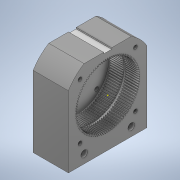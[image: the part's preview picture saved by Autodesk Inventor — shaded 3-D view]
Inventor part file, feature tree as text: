
AUTODESK INVENTOR PART (.ipt)
format: ipt  version: 2022 (Build 260153000, 153)  size: 1,526,272 bytes
history: mixed  units: mm
features: sketch x7, extrude x6, other x3, imported_body x1
ambient origin geometry x8: Origin, YZ Plane, XZ Plane, XY Plane, X Axis, Y Axis, Z Axis, Center Point
bodies: Solid1 (imported_parasolid)
feature tree (17):
  other  "Assembly2.iam"
  other  "96Gears_Stage_1_modified.ipt:1"
  other  "96Gears_Stage_2_modified.ipt:1"
  extrude  "Extrusion3"  Depth=3.0mm
  extrude  "Extrusion5"  Depth=1.0mm TaperAngle=0.0deg
  extrude  "Extrusion6"  Depth=6.0mm TaperAngle=0.0deg
  extrude  "Extrusion7"  TaperAngle=0.0deg  [1 undecoded]
  extrude  "Extrusion8"  Depth=3.5mm
  extrude  "Extrusion9"  Depth=5.0mm
  sketch  "Sketch5"  dims[d7=6.0mm d8=1.0mm d9=0.0mm]
  sketch  "Sketch4"  dims[d0=10.0mm d6=3.0mm]
  sketch  "Sketch7"  dims[d17=32.25mm d18=6.0mm d19=0.0mm]
  sketch  "Sketch8"  dims[d20=10.0mm d21=0.0mm d22=0.0mm]
  sketch  "Sketch9"  dims[d23=6.75mm d27=3.5mm]
  sketch  "Sketch10"  dims[d28=0.0mm d29=0.0mm d30=5.0mm]
  sketch  "Sketch11"  dims[d31=3.0mm d32=0.0mm d35=5.5mm d36=3.0mm d37=0.0mm]
  imported_body  NMx_Import_Brep_tag  [imported B-rep: ~806 faces, bbox_mm=[27.0, 66.5, 60.0]]
note: 1 required parameter value undecoded (feature->parameter linkage not recoverable at this tier; creation-order binding heuristic only, values carry confidence <= 0.55)
